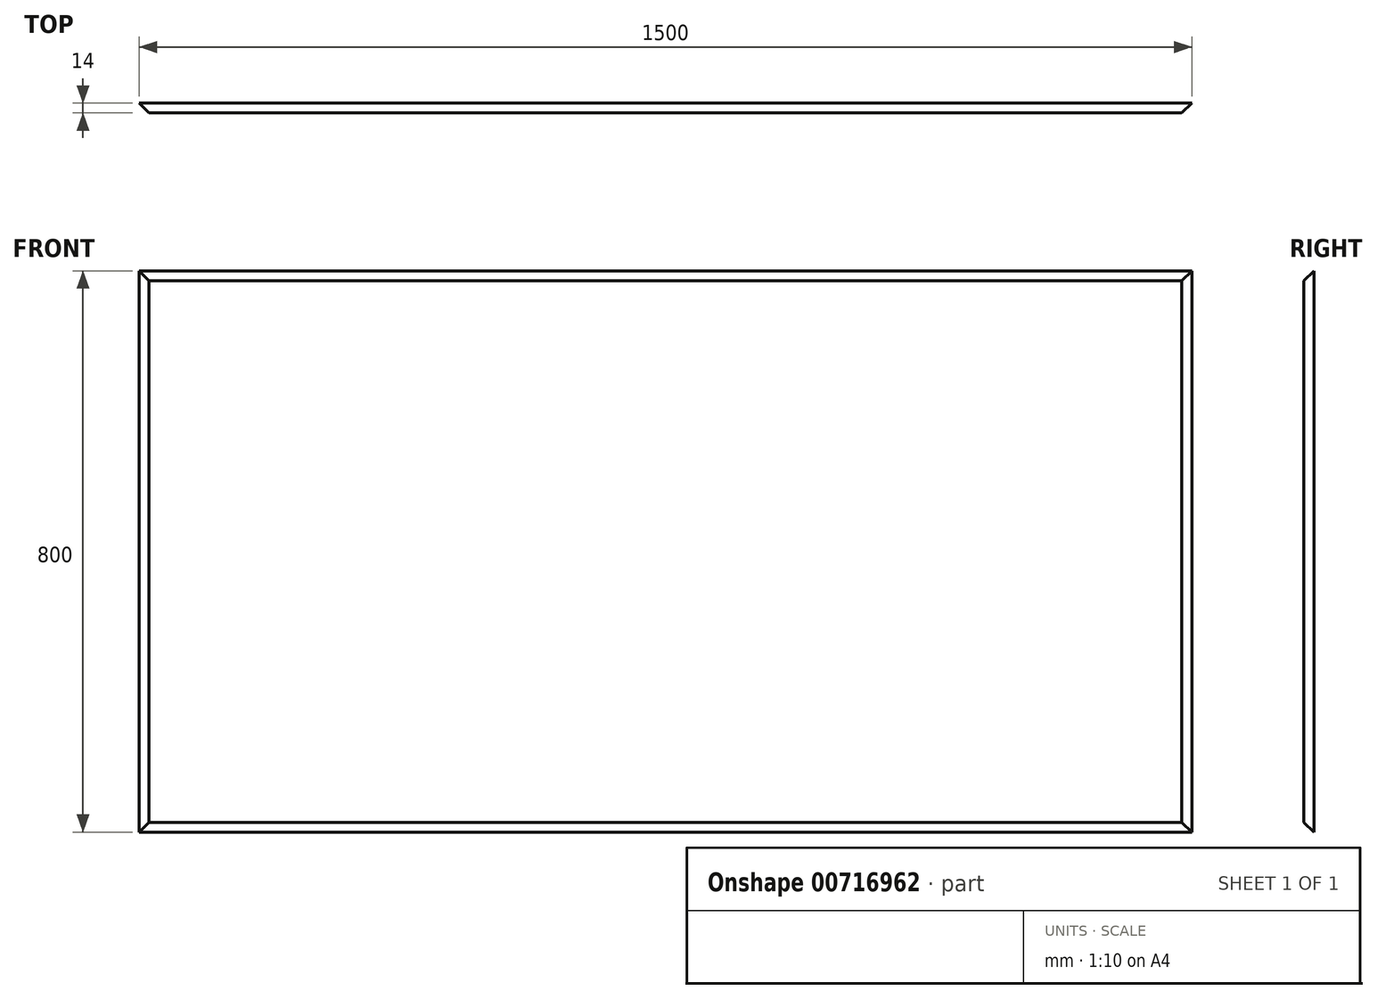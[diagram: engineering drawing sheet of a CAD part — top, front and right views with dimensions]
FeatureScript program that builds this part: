
annotation { "Feature Type Name" : "Feature", "Feature Type Description" : "" }
export const myFeature = defineFeature(function(context is Context, id is Id, definition is map)
    precondition{}
    {
        {
            var Q0;
            Q0=qCreatedBy(makeId("Front.planeOp"),FACE);
            var sketch = newSketch(context, id + "F0", { "sketchPlane" : qUnion([Q0])});
            skLineSegment(sketch, "E0.bottom", {"start": v(750, 400) * mm, "end": v(-750, 400) * mm});
            skLineSegment(sketch, "E0.top", {"start": v(750, -400) * mm, "end": v(-750, -400) * mm});
            skLineSegment(sketch, "E0.left", {"start": v(750, 400) * mm, "end": v(750, -400) * mm});
            skLineSegment(sketch, "E0.right", {"start": v(-750, 400) * mm, "end": v(-750, -400) * mm});
            skPoint(sketch, "E0.middle", {"position": v(0, 0) * mm});
            skSolve(sketch);
        }
        {
            var Q0;
            Q0=makeQuery(id+"F0.imprint","IMPRINT",FACE,{"disambiguationData":[TD([[makeQuery(id+"F0.imprint","IMPRINT",EDGE,{"derivedFrom":sQuery(id+"F0.wireOp",EDGE,"E0.bottom")}),1.0]])]});
            extrude(context, id + "F1", {"entities" : qUnion([Q0]), "depth" : 14 * mm, "offsetDistance" : 25 * mm});
        }
        {
            var Q0;
            Q0=makeQuery(id+"F1.opExtrude","CAP_FACE",FACE,{"disambiguationData":[OSD([sQuery(id+"F0.wireOp",EDGE,"E0.bottom"),sQuery(id+"F0.wireOp",EDGE,"E0.top"),sQuery(id+"F0.wireOp",EDGE,"E0.left"),sQuery(id+"F0.wireOp",EDGE,"E0.right")])],"isStart":false});
            chamfer(context, id + "F2", {"entities" : qUnion([Q0]), "width" : 14 * mm, "tangentPropagation" : true});
        }
    });
